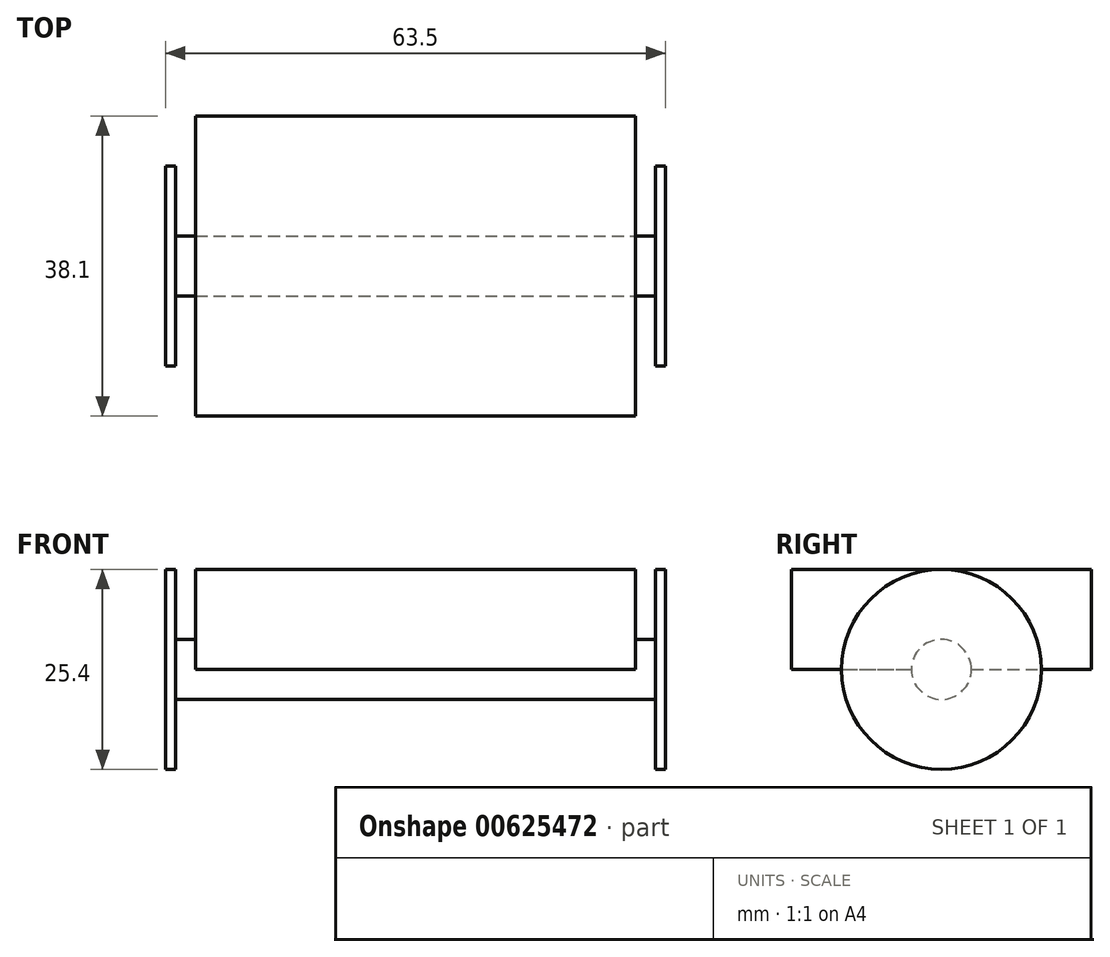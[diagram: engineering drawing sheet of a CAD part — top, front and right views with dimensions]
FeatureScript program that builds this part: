
annotation { "Feature Type Name" : "Feature", "Feature Type Description" : "" }
export const myFeature = defineFeature(function(context is Context, id is Id, definition is map)
    precondition{}
    {
        {
            var Q0;
            Q0=qCreatedBy(makeId("Front.planeOp"),FACE);
            var sketch = newSketch(context, id + "F0", { "sketchPlane" : qUnion([Q0])});
            skLineSegment(sketch, "E0.bottom", {"start": v(0, 0) * mm, "end": v(55.88, 0) * mm});
            skLineSegment(sketch, "E0.top", {"start": v(0, 12.7) * mm, "end": v(55.88, 12.7) * mm});
            skLineSegment(sketch, "E0.left", {"start": v(0, 0) * mm, "end": v(0, 12.7) * mm});
            skLineSegment(sketch, "E0.right", {"start": v(55.88, 0) * mm, "end": v(55.88, 12.7) * mm});
            skSolve(sketch);
        }
        {
            var Q0;
            Q0=makeQuery(id+"F0.imprint","IMPRINT",FACE,{"disambiguationData":[TD([[makeQuery(id+"F0.imprint","IMPRINT",EDGE,{"derivedFrom":sQuery(id+"F0.wireOp",EDGE,"E0.bottom")}),1.0]])]});
            extrude(context, id + "F1", {"entities" : qUnion([Q0]), "depth" : 38.1 * mm, "offsetDistance" : 25.4 * mm});
        }
        {
            var Q0;
            Q0=makeQuery(id+"F1.opExtrude","SWEPT_FACE",FACE,{"disambiguationData":[OSD([sQuery(id+"F0.wireOp",EDGE,"E0.right")])]});
            var sketch = newSketch(context, id + "F2", { "sketchPlane" : qUnion([Q0])});
            skCircle(sketch, "E1", {"center": v(-19.05, 0) * mm, "radius": 3.81 * mm});
            skSolve(sketch);
        }
        {
            var Q0;
            {var subQ0=sQuery(id+"F2.wireOp",EDGE,"E1");var subQ1=makeQuery(id+"F1.opExtrude","SWEPT_EDGE",EDGE,{"disambiguationData":[OSD([sQuery(id+"F0.wireOp",EDGE,"E0.bottom"),sQuery(id+"F0.wireOp",EDGE,"E0.right")])]});var subQ2=makeQuery(id+"F2.imprint","INTERSECT",VERTEX,{"disambiguationData":[OD(0.0)],"derivedFrom":[subQ1,subQ0]});Q0=makeQuery(id+"F2.imprint","IMPRINT",FACE,{"disambiguationData":[TD([[makeQuery(id+"F2.imprint","IMPRINT",EDGE,{"disambiguationData":[TD([[subQ2,-1.0]])],"derivedFrom":subQ0}),1.0]])]});}
            var Q1;
            {var subQ0=sQuery(id+"F2.wireOp",EDGE,"E1");var subQ1=makeQuery(id+"F1.opExtrude","SWEPT_EDGE",EDGE,{"disambiguationData":[OSD([sQuery(id+"F0.wireOp",EDGE,"E0.bottom"),sQuery(id+"F0.wireOp",EDGE,"E0.right")])]});var subQ2=makeQuery(id+"F2.imprint","INTERSECT",VERTEX,{"disambiguationData":[OD(0.0)],"derivedFrom":[subQ1,subQ0]});Q1=makeQuery(id+"F2.imprint","IMPRINT",FACE,{"disambiguationData":[TD([[makeQuery(id+"F2.imprint","IMPRINT",EDGE,{"disambiguationData":[TD([[subQ2,1.0]])],"derivedFrom":subQ0}),1.0]])]});}
            extrude(context, id + "F3", {"entities" : qUnion([Q0, Q1]), "operationType" : NewBodyOperationType.ADD, "oppositeDirection" : true, "depth" : 58.42 * mm, "offsetDistance" : 25.4 * mm});
        }
        {
            var Q0;
            Q0 = qSketchRegion(id + "F2", true);
            extrude(context, id + "F4", {"entities" : qUnion([Q0]), "operationType" : NewBodyOperationType.ADD, "depth" : 2.54 * mm, "offsetDistance" : 25.4 * mm});
        }
        {
            var Q0;
            Q0=makeQuery(id+"F3.opExtrude","CAP_FACE",FACE,{"disambiguationData":[OSD([sQuery(id+"F2.wireOp",EDGE,"E1")])],"isStart":false});
            var sketch = newSketch(context, id + "F5", { "sketchPlane" : qUnion([Q0])});
            skCircle(sketch, "E2", {"center": v(19.05, 0) * mm, "radius": 12.7 * mm});
            skSolve(sketch);
        }
        {
            var Q0;
            Q0 = qSketchRegion(id + "F5", true);
            extrude(context, id + "F6", {"entities" : qUnion([Q0]), "operationType" : NewBodyOperationType.ADD, "depth" : 1.27 * mm, "offsetDistance" : 25.4 * mm});
        }
        {
            var Q0;
            Q0=makeQuery(id+"F4.opExtrude","CAP_FACE",FACE,{"disambiguationData":[OSD([sQuery(id+"F2.wireOp",EDGE,"E1")])],"isStart":false});
            var sketch = newSketch(context, id + "F7", { "sketchPlane" : qUnion([Q0])});
            skCircle(sketch, "E3", {"center": v(-19.05, 0) * mm, "radius": 12.7 * mm});
            skSolve(sketch);
        }
        {
            var Q0;
            Q0 = qSketchRegion(id + "F7", true);
            extrude(context, id + "F8", {"entities" : qUnion([Q0]), "operationType" : NewBodyOperationType.ADD, "depth" : 1.27 * mm, "offsetDistance" : 25.4 * mm});
        }
    });
